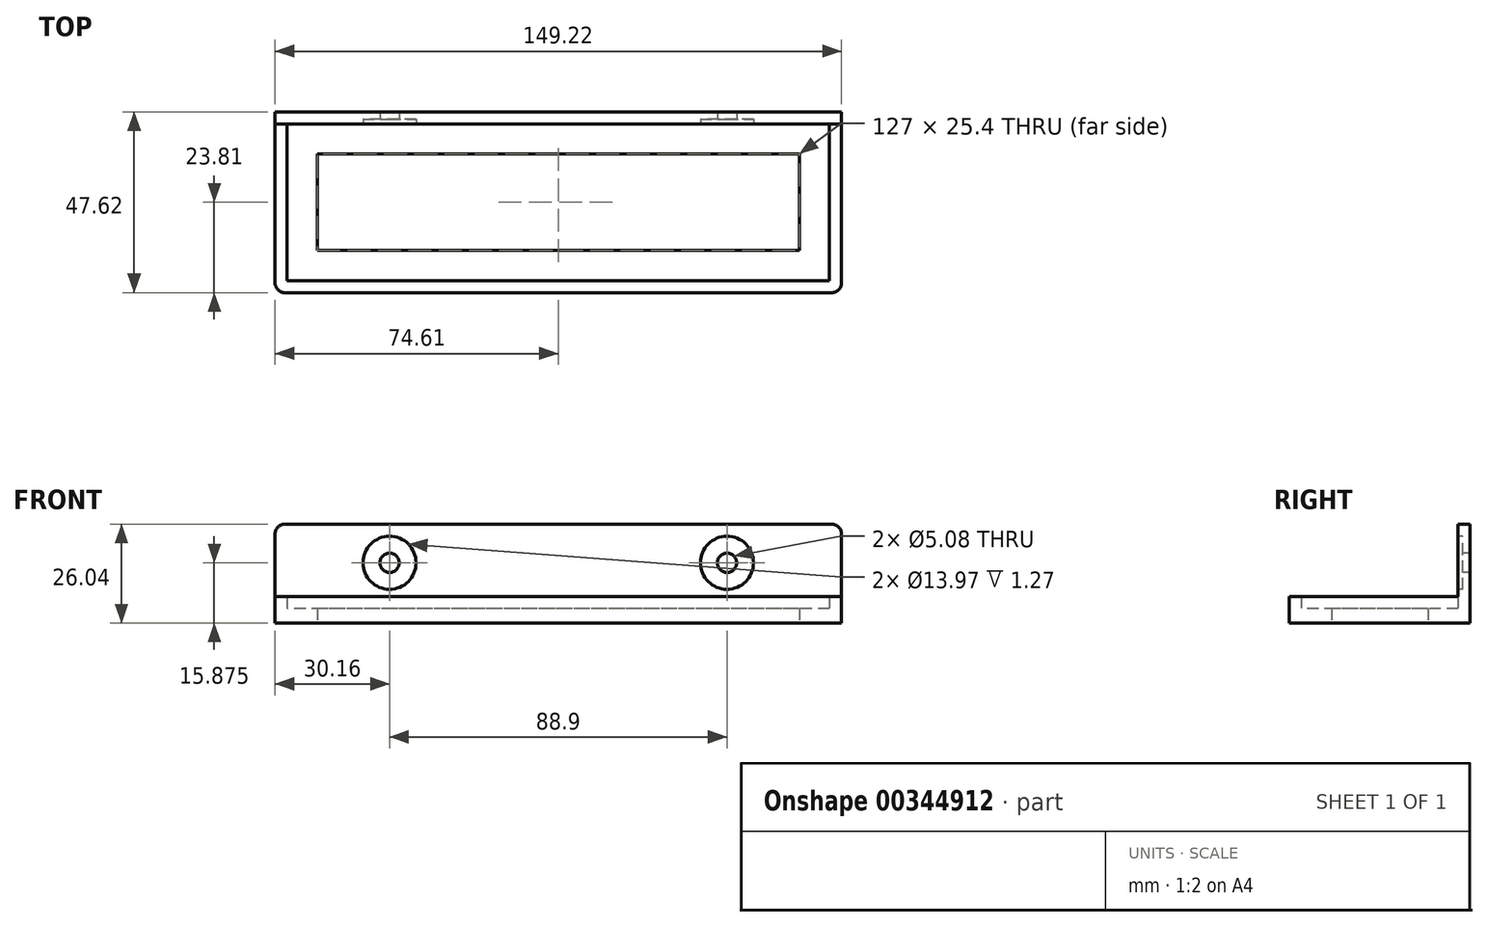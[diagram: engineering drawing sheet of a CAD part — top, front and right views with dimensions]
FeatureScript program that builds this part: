
annotation { "Feature Type Name" : "Feature", "Feature Type Description" : "" }
export const myFeature = defineFeature(function(context is Context, id is Id, definition is map)
    precondition{}
    {
        {
            var Q0;
            Q0=qCreatedBy(makeId("Top.planeOp"),FACE);
            var sketch = newSketch(context, id + "F0", { "sketchPlane" : qUnion([Q0])});
            skLineSegment(sketch, "E0.bottom", {"start": v(74.61, 23.81) * mm, "end": v(-74.61, 23.81) * mm});
            skLineSegment(sketch, "E0.top", {"start": v(74.61, -23.81) * mm, "end": v(-74.61, -23.81) * mm});
            skLineSegment(sketch, "E0.left", {"start": v(74.61, 23.81) * mm, "end": v(74.61, -23.81) * mm});
            skLineSegment(sketch, "E0.right", {"start": v(-74.61, 23.81) * mm, "end": v(-74.61, -23.81) * mm});
            skPoint(sketch, "E0.middle", {"position": v(0, 0) * mm});
            skLineSegment(sketch, "E1.bottom", {"start": v(63.5, 12.7) * mm, "end": v(-63.5, 12.7) * mm});
            skLineSegment(sketch, "E1.top", {"start": v(63.5, -12.7) * mm, "end": v(-63.5, -12.7) * mm});
            skLineSegment(sketch, "E1.left", {"start": v(63.5, 12.7) * mm, "end": v(63.5, -12.7) * mm});
            skLineSegment(sketch, "E1.right", {"start": v(-63.5, 12.7) * mm, "end": v(-63.5, -12.7) * mm});
            skSolve(sketch);
        }
        {
            var Q0;
            Q0=makeQuery(id+"F0.imprint","IMPRINT",FACE,{"disambiguationData":[TD([[makeQuery(id+"F0.imprint","IMPRINT",EDGE,{"derivedFrom":sQuery(id+"F0.wireOp",EDGE,"E0.bottom")}),1.0]])]});
            extrude(context, id + "F1", {"entities" : qUnion([Q0]), "depth" : 3.8 * mm});
        }
        {
            var Q0;
            Q0=makeQuery(id+"F1.opExtrude","CAP_FACE",FACE,{"disambiguationData":[OSD([sQuery(id+"F0.wireOp",EDGE,"E0.bottom"),sQuery(id+"F0.wireOp",EDGE,"E0.top"),sQuery(id+"F0.wireOp",EDGE,"E0.left"),sQuery(id+"F0.wireOp",EDGE,"E0.right"),sQuery(id+"F0.wireOp",EDGE,"E1.bottom"),sQuery(id+"F0.wireOp",EDGE,"E1.top"),sQuery(id+"F0.wireOp",EDGE,"E1.left"),sQuery(id+"F0.wireOp",EDGE,"E1.right")])],"isStart":false});
            var sketch = newSketch(context, id + "F2", { "sketchPlane" : qUnion([Q0])});
            skLineSegment(sketch, "E2.bottom", {"start": v(74.61, 23.81) * mm, "end": v(-74.61, 23.81) * mm});
            skLineSegment(sketch, "E2.top", {"start": v(74.61, -23.81) * mm, "end": v(-74.61, -23.81) * mm});
            skLineSegment(sketch, "E2.left", {"start": v(74.61, 23.81) * mm, "end": v(74.61, -23.81) * mm});
            skLineSegment(sketch, "E2.right", {"start": v(-74.61, 23.81) * mm, "end": v(-74.61, -23.81) * mm});
            skPoint(sketch, "E2.middle", {"position": v(0, 0) * mm});
            skLineSegment(sketch, "E3.bottom", {"start": v(71.44, 20.64) * mm, "end": v(-71.44, 20.64) * mm});
            skLineSegment(sketch, "E3.top", {"start": v(71.44, -20.64) * mm, "end": v(-71.44, -20.64) * mm});
            skLineSegment(sketch, "E3.left", {"start": v(71.44, 20.64) * mm, "end": v(71.44, -20.64) * mm});
            skLineSegment(sketch, "E3.right", {"start": v(-71.44, 20.64) * mm, "end": v(-71.44, -20.64) * mm});
            skSolve(sketch);
        }
        {
            var Q0;
            Q0=makeQuery(id+"F2.imprint","IMPRINT",FACE,{"disambiguationData":[TD([[makeQuery(id+"F2.imprint","IMPRINT",EDGE,{"derivedFrom":sQuery(id+"F2.wireOp",EDGE,"E2.bottom")}),1.0]])]});
            extrude(context, id + "F3", {"entities" : qUnion([Q0]), "operationType" : NewBodyOperationType.ADD, "depth" : 3.17 * mm});
        }
        {
            var Q0;
            Q0=makeQuery(id+"F3.opExtrude","CAP_FACE",FACE,{"disambiguationData":[OSD([sQuery(id+"F2.wireOp",EDGE,"E2.bottom"),sQuery(id+"F2.wireOp",EDGE,"E2.top"),sQuery(id+"F2.wireOp",EDGE,"E2.left"),sQuery(id+"F2.wireOp",EDGE,"E2.right"),sQuery(id+"F2.wireOp",EDGE,"E3.bottom"),sQuery(id+"F2.wireOp",EDGE,"E3.top"),sQuery(id+"F2.wireOp",EDGE,"E3.left"),sQuery(id+"F2.wireOp",EDGE,"E3.right")])],"isStart":false});
            var sketch = newSketch(context, id + "F4", { "sketchPlane" : qUnion([Q0])});
            skLineSegment(sketch, "E4.bottom", {"start": v(-74.61, 23.81) * mm, "end": v(74.61, 23.81) * mm});
            skLineSegment(sketch, "E4.top", {"start": v(-74.61, 20.64) * mm, "end": v(74.61, 20.64) * mm});
            skLineSegment(sketch, "E4.left", {"start": v(-74.61, 23.81) * mm, "end": v(-74.61, 20.64) * mm});
            skLineSegment(sketch, "E4.right", {"start": v(74.61, 23.81) * mm, "end": v(74.61, 20.64) * mm});
            skSolve(sketch);
        }
        {
            var Q0;
            Q0=makeQuery(id+"F4.imprint","IMPRINT",FACE,{"disambiguationData":[TD([[makeQuery(id+"F4.imprint","IMPRINT",EDGE,{"derivedFrom":sQuery(id+"F4.wireOp",EDGE,"E4.bottom")}),1.0]])]});
            extrude(context, id + "F5", {"entities" : qUnion([Q0]), "operationType" : NewBodyOperationType.ADD, "depth" : 19.05 * mm});
        }
        {
            var Q0;
            Q0=makeQuery(id+"F5.boolean.opBoolean","MERGE",FACE,{"derivedFrom":[makeQuery(id+"F3.opExtrude","SWEPT_FACE",FACE,{"disambiguationData":[OSD([sQuery(id+"F2.wireOp",EDGE,"E3.bottom")])]}),makeQuery(id+"F5.opExtrude","SWEPT_FACE",FACE,{"disambiguationData":[OSD([sQuery(id+"F4.wireOp",EDGE,"E4.top")])]})]});
            var sketch = newSketch(context, id + "F6", { "sketchPlane" : qUnion([Q0])});
            skCircle(sketch, "E5", {"center": v(-44.45, 15.88) * mm, "radius": 6.99 * mm});
            skCircle(sketch, "E6", {"center": v(44.45, 15.88) * mm, "radius": 6.99 * mm});
            skCircle(sketch, "E7", {"center": v(-44.45, 15.88) * mm, "radius": 2.54 * mm});
            skCircle(sketch, "E8", {"center": v(44.45, 15.88) * mm, "radius": 2.54 * mm});
            skSolve(sketch);
        }
        {
            var Q0;
            Q0=makeQuery(id+"F6.imprint","IMPRINT",FACE,{"disambiguationData":[TD([[makeQuery(id+"F6.imprint","IMPRINT",EDGE,{"derivedFrom":sQuery(id+"F6.wireOp",EDGE,"E7")}),1.0]])]});
            var Q1;
            Q1=makeQuery(id+"F6.imprint","IMPRINT",FACE,{"disambiguationData":[TD([[makeQuery(id+"F6.imprint","IMPRINT",EDGE,{"derivedFrom":sQuery(id+"F6.wireOp",EDGE,"E8")}),1.0]])]});
            extrude(context, id + "F7", {"entities" : qUnion([Q0, Q1]), "operationType" : NewBodyOperationType.REMOVE, "oppositeDirection" : true, "depth" : 25.4 * mm});
        }
        {
            var Q0;
            Q0 = qSketchRegion(id + "F6", true);
            extrude(context, id + "F8", {"entities" : qUnion([Q0]), "operationType" : NewBodyOperationType.REMOVE, "oppositeDirection" : true, "depth" : 1.27 * mm});
        }
        {
            var Q0;
            {var subQ3=sQuery(id+"F4.wireOp",EDGE,"E4.top");Q0=makeQuery(id+"F5.boolean.opBoolean","SPLIT",EDGE,{"disambiguationData":[TD([makeQuery(id+"F1.opExtrude","SWEPT_FACE",FACE,{"disambiguationData":[OSD([sQuery(id+"F0.wireOp",EDGE,"E0.right")])]})])],"derivedFrom":makeQuery(id+"F5.opExtrude","CAP_EDGE",EDGE,{"disambiguationData":[OSD([subQ3])],"isStart":true})});}
            var Q1;
            Q1=makeQuery(id+"F3.opExtrude","CAP_EDGE",EDGE,{"disambiguationData":[OSD([sQuery(id+"F2.wireOp",EDGE,"E3.bottom")])],"isStart":true});
            var Q2;
            {var subQ3=sQuery(id+"F4.wireOp",EDGE,"E4.top");Q2=makeQuery(id+"F5.boolean.opBoolean","SPLIT",EDGE,{"disambiguationData":[TD([makeQuery(id+"F1.opExtrude","SWEPT_FACE",FACE,{"disambiguationData":[OSD([sQuery(id+"F0.wireOp",EDGE,"E0.left")])]})])],"derivedFrom":makeQuery(id+"F5.opExtrude","CAP_EDGE",EDGE,{"disambiguationData":[OSD([subQ3])],"isStart":true})});}
            var Q3;
            Q3=makeQuery(id+"F5.opExtrude","CAP_EDGE",EDGE,{"disambiguationData":[OSD([sQuery(id+"F4.wireOp",EDGE,"E4.right")])],"isStart":false});
            var Q4;
            Q4=makeQuery(id+"F5.opExtrude","CAP_EDGE",EDGE,{"disambiguationData":[OSD([sQuery(id+"F4.wireOp",EDGE,"E4.left")])],"isStart":false});
            var Q5;
            Q5=makeQuery(id+"F3.boolean.opBoolean","MERGE",EDGE,{"derivedFrom":[makeQuery(id+"F1.opExtrude","SWEPT_EDGE",EDGE,{"disambiguationData":[OSD([sQuery(id+"F0.wireOp",EDGE,"E0.top"),sQuery(id+"F0.wireOp",EDGE,"E0.right")])]}),makeQuery(id+"F3.opExtrude","SWEPT_EDGE",EDGE,{"disambiguationData":[OSD([sQuery(id+"F2.wireOp",EDGE,"E2.top"),sQuery(id+"F2.wireOp",EDGE,"E2.right")])]})]});
            var Q6;
            Q6=makeQuery(id+"F3.boolean.opBoolean","MERGE",EDGE,{"derivedFrom":[makeQuery(id+"F1.opExtrude","SWEPT_EDGE",EDGE,{"disambiguationData":[OSD([sQuery(id+"F0.wireOp",EDGE,"E0.top"),sQuery(id+"F0.wireOp",EDGE,"E0.left")])]}),makeQuery(id+"F3.opExtrude","SWEPT_EDGE",EDGE,{"disambiguationData":[OSD([sQuery(id+"F2.wireOp",EDGE,"E2.top"),sQuery(id+"F2.wireOp",EDGE,"E2.left")])]})]});
            var Q7;
            Q7=makeQuery(id+"F3.opExtrude","CAP_EDGE",EDGE,{"disambiguationData":[OSD([sQuery(id+"F2.wireOp",EDGE,"E3.left")])],"isStart":true});
            var Q8;
            Q8=makeQuery(id+"F3.opExtrude","CAP_EDGE",EDGE,{"disambiguationData":[OSD([sQuery(id+"F2.wireOp",EDGE,"E3.right")])],"isStart":true});
            var Q9;
            Q9=makeQuery(id+"F3.opExtrude","CAP_EDGE",EDGE,{"disambiguationData":[OSD([sQuery(id+"F2.wireOp",EDGE,"E3.top")])],"isStart":true});
            fillet(context, id + "F9", {"entities" : qUnion([Q0, Q1, Q2, Q3, Q4, Q5, Q6, Q7, Q8, Q9]), "radius" : 2.54 * mm, "tangentPropagation" : true, "allowEdgeOverflow" : false});
        }
    });
